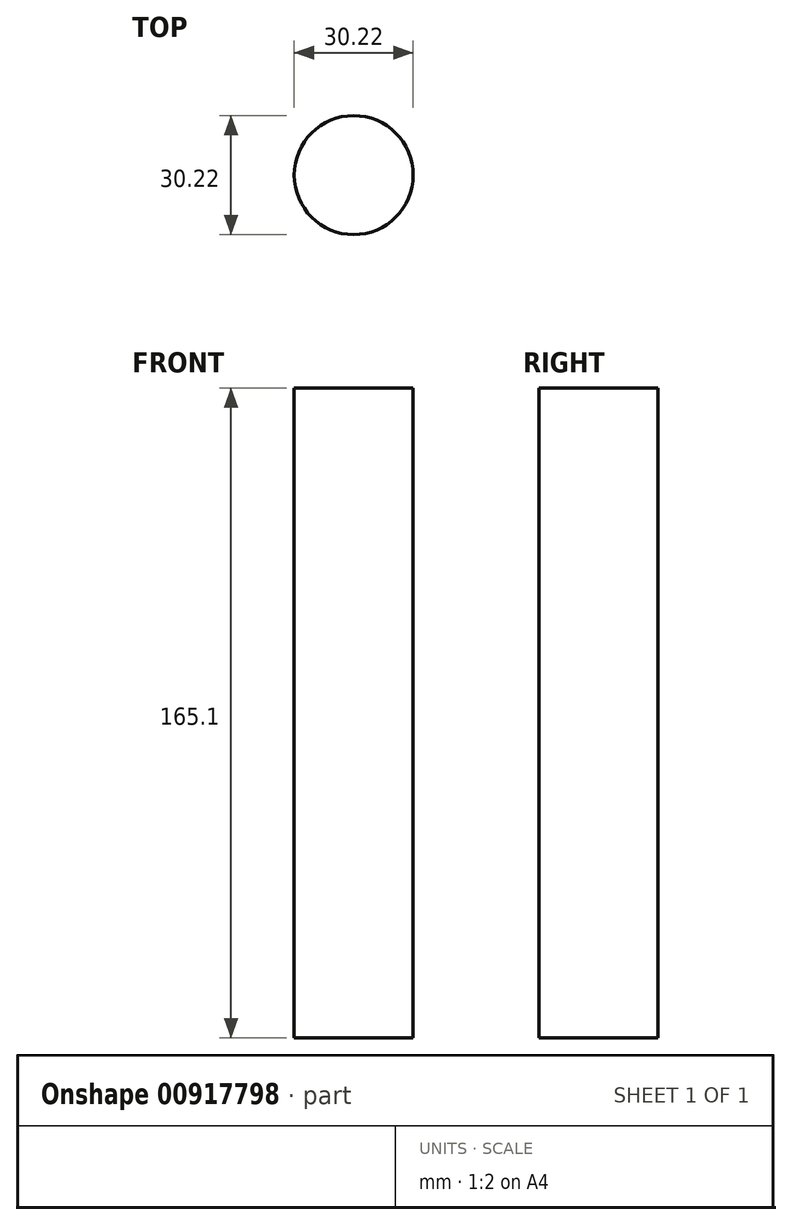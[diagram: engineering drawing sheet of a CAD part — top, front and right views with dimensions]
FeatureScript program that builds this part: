
annotation { "Feature Type Name" : "Feature", "Feature Type Description" : "" }
export const myFeature = defineFeature(function(context is Context, id is Id, definition is map)
    precondition{}
    {
        {
            var Q0;
            Q0=qCreatedBy(makeId("Top.planeOp"),FACE);
            var sketch = newSketch(context, id + "F0", { "sketchPlane" : qUnion([Q0])});
            skCircle(sketch, "E0", {"center": v(0, 0) * mm, "radius": 15.11 * mm});
            skSolve(sketch);
        }
        {
            var Q0;
            Q0=makeQuery(id+"F0.imprint","IMPRINT",FACE,{"disambiguationData":[TD([[makeQuery(id+"F0.imprint","IMPRINT",EDGE,{"derivedFrom":sQuery(id+"F0.wireOp",EDGE,"E0")}),1.0]])]});
            extrude(context, id + "F1", {"entities" : qUnion([Q0]), "surfaceOperationType" : NewSurfaceOperationType.ADD, "depth" : 165.1 * mm, "offsetDistance" : 25.4 * mm});
        }
    });
